# Revit family: Противоподкопное ограждение
name_source: partatom
category: Специальное оборудование
units: mm (PartAtom-declared; Revit-internal decimal feet)

## family parameters
Общий = Нет
При загрузке вырезать с полостями = Нет
Размер круглого соединителя = Использовать диаметр
Тип детали = Нормальный
Точка расчета площади = Нет

## types (10) — shared parameters
ADSK_Единица измерения = м.
ADSK_Завод-изготовитель = FENSYS
URL = https://www.fensys.ru
Группа модели = Противоподкоп
Изготовитель = FENSYS

## per-type parameters (varying)
| type | ADSK_Наименование | D прутка | Пруток ф16 | Ширина панели |
| Для панелей 2400_пруток Ф8 | Противоподкоп для панелей шириной 2400, Ф8 | 8 | Нет | 2250 мм |
| Для панелей 2500_пруток Ф8 | Противоподкоп для панелей шириной 2500, Ф8 | 8 | Нет | 2400 мм |
| Для панелей 3000_пруток Ф8 | Противоподкоп для панелей шириной 3000, Ф8 | 8 | Нет | 2850 мм |
| Для панелей 3100_пруток Ф8 | Противоподкоп для панелей шириной 3100, Ф8 | 8 | Нет | 3000 мм |
| Свободный размер_пруток Ф8 | Противоподкоп для ширины 3100, Ф18 | 8 | Нет | 3100 мм |
| Для панелей 2400_пруток Ф16 | Противоподкоп для панелей шириной 2400, Ф16 | 16 | Да | 2250 мм |
| Для панелей 2500_пруток Ф16 | Противоподкоп для панелей шириной 2500, Ф16 | 16 | Да | 2400 мм |
| Для панелей 3000_пруток Ф16 | Противоподкоп для панелей шириной 3000, Ф16 | 16 | Да | 2850 мм |
| Для панелей 3100_пруток Ф16 | Противоподкоп для панелей шириной 3100, Ф16 | 16 | Да | 3000 мм |
| Свободный размер_пруток Ф16 | Противоподкоп для шириы 3000, Ф16 | 16 | Да | 3000 мм |
